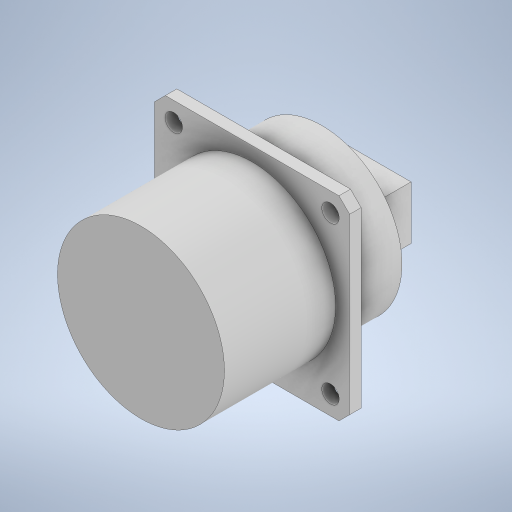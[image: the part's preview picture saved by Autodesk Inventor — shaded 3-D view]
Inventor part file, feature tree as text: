
AUTODESK INVENTOR PART (.ipt)
format: ipt  version: 2023 (Build 270158000, 158)  size: 277,504 bytes
history: native  units: in
note: dims shown in document units (in); Inventor stores cm internally (conversion verified against a paired STEP export)
features: sketch x5, extrude x4, chamfer x1, hole x1
ambient origin geometry x8: Origin, YZ Plane, XZ Plane, XY Plane, X Axis, Y Axis, Z Axis, Center Point
bodies: Solid1 (feature_tree)
feature tree (11):
  extrude  "Extrusion1"  Depth=1.4382in
  chamfer  "Chamfer1"  Distance=0.085in
  hole  "Hole1"  [1 undecoded]
  extrude  "Extrusion2"  Depth=1.2303in
  extrude  "Extrusion3"  Depth=0.8201in
  extrude  "Extrusion4"  Depth=0.5906in
  sketch  "Sketch1"  dims[d0=1.4382in d1=1.4382in d2=0.085in d3=0.0in]
  sketch  "Sketch2"  dims[d4=0.0787in d5=0.0787in d6=45.0deg d7=1.1559in]
  sketch  "Sketch3"  dims[d8=0.128in d9=0.2362in d10=0.1575in d11=0.0787in d12=90.0deg d13=0.315in d14=0.8108in d15=1.2303in]
  sketch  "Sketch4"  dims[d16=0.8201in d17=0.0in d18=1.1811in]
  sketch  "Sketch5"  dims[d19=0.4291in d20=0.0in d21=0.5906in d22=0.3937in d23=0.3626in d24=0.0in]
note: 1 required parameter value undecoded (feature->parameter linkage not recoverable at this tier; creation-order binding heuristic only, values carry confidence <= 0.55)
